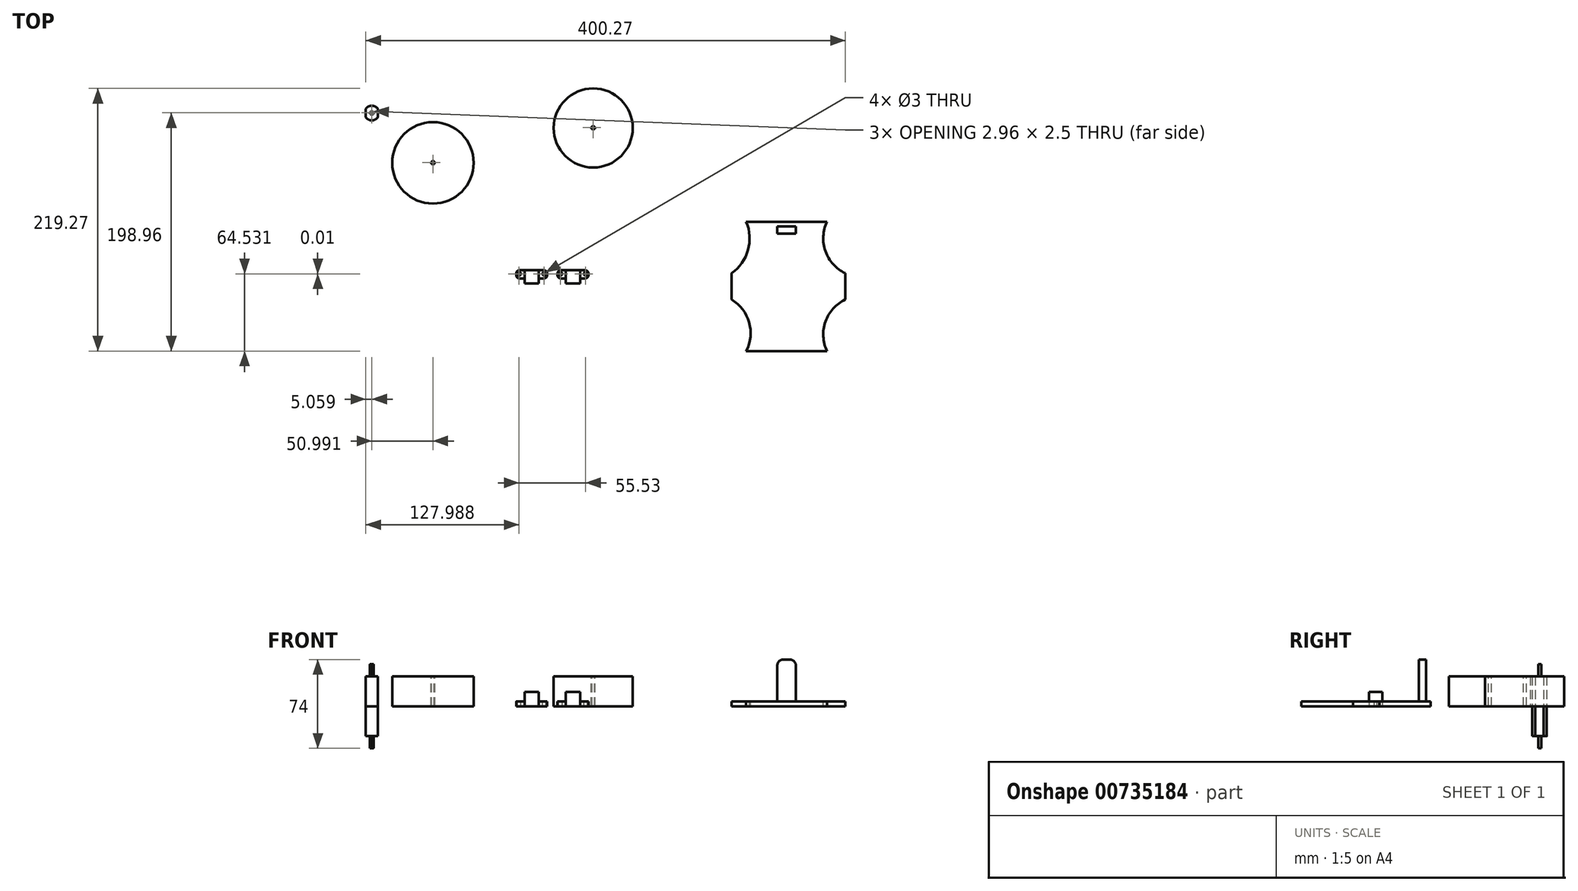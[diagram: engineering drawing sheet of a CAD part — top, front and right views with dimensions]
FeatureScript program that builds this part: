
annotation { "Feature Type Name" : "Feature", "Feature Type Description" : "" }
export const myFeature = defineFeature(function(context is Context, id is Id, definition is map)
    precondition{}
    {
        {
            var Q0;
            Q0=qCreatedBy(makeId("Top.planeOp"),FACE);
            var sketch = newSketch(context, id + "F0", { "sketchPlane" : qUnion([Q0])});
            skCircle(sketch, "E0", {"center": v(0, 0) * mm, "radius": 34 * mm});
            skSolve(sketch);
        }
        {
            var Q0;
            Q0=makeQuery(id+"F0.imprint","IMPRINT",FACE,{"disambiguationData":[TD([[makeQuery(id+"F0.imprint","IMPRINT",EDGE,{"derivedFrom":sQuery(id+"F0.wireOp",EDGE,"E0")}),1.0]])]});
            extrude(context, id + "F1", {"entities" : qUnion([Q0]), "depth" : 25 * mm, "offsetDistance" : 25 * mm});
        }
        {
            var Q0;
            Q0=qCreatedBy(makeId("Top.planeOp"),FACE);
            var sketch = newSketch(context, id + "F2", { "sketchPlane" : qUnion([Q0])});
            skArc(sketch, "E1", {"start": v(-56.05, 38.17) * mm, "mid": v(-51, 35.48) * mm, "end": v(-45.93, 38.17) * mm});
            skLineSegment(sketch, "E2", {"start": v(-56.05, 45) * mm, "end": v(-56.05, 38.17) * mm});
            skLineSegment(sketch, "E3", {"start": v(-45.93, 45) * mm, "end": v(-45.93, 38.17) * mm});
            skArc(sketch, "E4.trimOffspring", {"start": v(-45.93, 45) * mm, "mid": v(-51, 47.68) * mm, "end": v(-56.05, 45) * mm});
            skSolve(sketch);
        }
        {
            var Q0;
            Q0=makeQuery(id+"F1.opExtrude","CAP_FACE",FACE,{"disambiguationData":[OSD([sQuery(id+"F0.wireOp",EDGE,"E0")])],"isStart":false});
            var sketch = newSketch(context, id + "F3", { "sketchPlane" : qUnion([Q0])});
            skArc(sketch, "E5", {"start": v(1.12, -1) * mm, "mid": v(0, 1.5) * mm, "end": v(-1.12, -1) * mm});
            skLineSegment(sketch, "E6", {"start": v(0, -1) * mm, "end": v(-1.12, -1) * mm});
            skLineSegment(sketch, "E7", {"start": v(-1.12, -1) * mm, "end": v(1.12, -1) * mm});
            skSolve(sketch);
        }
        {
            var Q0;
            {var subQ0=sQuery(id+"F3.wireOp",EDGE,"E5");Q0=makeQuery(id+"F3.imprint","IMPRINT",FACE,{"disambiguationData":[TD([[makeQuery(id+"F3.imprint","IMPRINT",EDGE,{"derivedFrom":subQ0}),1.0]])]});}
            extrude(context, id + "F4", {"entities" : qUnion([Q0]), "operationType" : NewBodyOperationType.REMOVE, "oppositeDirection" : true, "depth" : 44 * mm, "offsetDistance" : 25 * mm});
        }
        {
            var Q0;
            Q0=makeQuery(id+"F2.imprint","IMPRINT",FACE,{"disambiguationData":[TD([[makeQuery(id+"F2.imprint","IMPRINT",EDGE,{"derivedFrom":sQuery(id+"F2.wireOp",EDGE,"E1")}),1.0]])]});
            extrude(context, id + "F5", {"entities" : qUnion([Q0]), "depth" : 25 * mm, "offsetDistance" : 25 * mm});
        }
        {
            var Q0;
            Q0=makeQuery(id+"F5.opExtrude","CAP_FACE",FACE,{"disambiguationData":[OSD([sQuery(id+"F2.wireOp",EDGE,"E1"),sQuery(id+"F2.wireOp",EDGE,"E2"),sQuery(id+"F2.wireOp",EDGE,"E3"),sQuery(id+"F2.wireOp",EDGE,"E4.trimOffspring")])],"isStart":false});
            var sketch = newSketch(context, id + "F6", { "sketchPlane" : qUnion([Q0])});
            skArc(sketch, "E8", {"start": v(-49.87, 40.58) * mm, "mid": v(-51, 43.08) * mm, "end": v(-52.1, 40.58) * mm});
            skLineSegment(sketch, "E9", {"start": v(-51, 40.58) * mm, "end": v(-52.1, 40.58) * mm});
            skLineSegment(sketch, "E10", {"start": v(-52.1, 40.58) * mm, "end": v(-49.87, 40.58) * mm});
            skSolve(sketch);
        }
        {
            var Q0;
            {var subQ0=sQuery(id+"F6.wireOp",EDGE,"E8");Q0=makeQuery(id+"F6.imprint","IMPRINT",FACE,{"disambiguationData":[TD([[makeQuery(id+"F6.imprint","IMPRINT",EDGE,{"derivedFrom":subQ0}),1.0]])]});}
            extrude(context, id + "F7", {"entities" : qUnion([Q0]), "operationType" : NewBodyOperationType.ADD, "depth" : 10 * mm, "offsetDistance" : 25 * mm});
        }
        {
            var Q0;
            Q0=qCreatedBy(makeId("Top.planeOp"),FACE);
            var sketch = newSketch(context, id + "F8", { "sketchPlane" : qUnion([Q0])});
            skCircle(sketch, "E11", {"center": v(133.78, 29.14) * mm, "radius": 33 * mm});
            skSolve(sketch);
        }
        {
            var Q0;
            Q0=makeQuery(id+"F8.imprint","IMPRINT",FACE,{"disambiguationData":[TD([[makeQuery(id+"F8.imprint","IMPRINT",EDGE,{"derivedFrom":sQuery(id+"F8.wireOp",EDGE,"E11")}),1.0]])]});
            extrude(context, id + "F9", {"entities" : qUnion([Q0]), "depth" : 25 * mm, "offsetDistance" : 25 * mm});
        }
        {
            var Q0;
            Q0=makeQuery(id+"F9.opExtrude","CAP_FACE",FACE,{"disambiguationData":[OSD([sQuery(id+"F8.wireOp",EDGE,"E11")])],"isStart":false});
            var sketch = newSketch(context, id + "F10", { "sketchPlane" : qUnion([Q0])});
            skArc(sketch, "E12", {"start": v(134.9, 28.14) * mm, "mid": v(133.78, 30.64) * mm, "end": v(132.66, 28.14) * mm});
            skLineSegment(sketch, "E13", {"start": v(133.77, 28.14) * mm, "end": v(132.66, 28.14) * mm});
            skLineSegment(sketch, "E14", {"start": v(132.66, 28.14) * mm, "end": v(134.9, 28.14) * mm});
            skSolve(sketch);
        }
        {
            var Q0;
            {var subQ0=sQuery(id+"F10.wireOp",EDGE,"E12");Q0=makeQuery(id+"F10.imprint","IMPRINT",FACE,{"disambiguationData":[TD([[makeQuery(id+"F10.imprint","IMPRINT",EDGE,{"derivedFrom":subQ0}),1.0]])]});}
            extrude(context, id + "F11", {"entities" : qUnion([Q0]), "operationType" : NewBodyOperationType.REMOVE, "oppositeDirection" : true, "depth" : 28.1 * mm, "offsetDistance" : 25 * mm});
        }
        {
            var Q0;
            Q0=makeQuery(id+"F5.opExtrude","SWEPT_BODY",BODY,{"disambiguationData":[OSD([sQuery(id+"F2.wireOp",EDGE,"E1"),sQuery(id+"F2.wireOp",EDGE,"E2"),sQuery(id+"F2.wireOp",EDGE,"E3"),sQuery(id+"F2.wireOp",EDGE,"E4.trimOffspring")])]});
            var Q1;
            Q1=qCreatedBy(makeId("Top.planeOp"),FACE);
            mirror(context, id + "F12", {"operationType" : NewBodyOperationType.ADD, "entities" : qUnion([Q0]), "mirrorPlane" : qUnion([Q1])});
        }
        {
            var Q0;
            Q0=qCreatedBy(makeId("Top.planeOp"),FACE);
            var sketch = newSketch(context, id + "F13", { "sketchPlane" : qUnion([Q0])});
            skLineSegment(sketch, "E15", {"start": v(249.22, -49.13) * mm, "end": v(249.22, -157.13) * mm});
            skLineSegment(sketch, "E16", {"start": v(249.22, -157.13) * mm, "end": v(344.22, -157.13) * mm});
            skLineSegment(sketch, "E17", {"start": v(344.22, -157.13) * mm, "end": v(344.22, -49.13) * mm});
            skLineSegment(sketch, "E18", {"start": v(249.22, -49.13) * mm, "end": v(344.22, -49.13) * mm});
            skSolve(sketch);
        }
        {
            var Q0;
            Q0=makeQuery(id+"F13.imprint","IMPRINT",FACE,{"disambiguationData":[TD([[makeQuery(id+"F13.imprint","IMPRINT",EDGE,{"derivedFrom":sQuery(id+"F13.wireOp",EDGE,"E15")}),1.0]])]});
            extrude(context, id + "F14", {"entities" : qUnion([Q0]), "depth" : 4 * mm, "offsetDistance" : 25 * mm});
        }
        {
            var Q0;
            Q0=makeQuery(id+"F14.opExtrude","CAP_FACE",FACE,{"disambiguationData":[OSD([sQuery(id+"F13.wireOp",EDGE,"E15"),sQuery(id+"F13.wireOp",EDGE,"E16"),sQuery(id+"F13.wireOp",EDGE,"E17"),sQuery(id+"F13.wireOp",EDGE,"E18")])],"isStart":false});
            var sketch = newSketch(context, id + "F15", { "sketchPlane" : qUnion([Q0])});
            skLineSegment(sketch, "E19", {"start": v(249.22, -49.13) * mm, "end": v(249.22, -92.13) * mm});
            skLineSegment(sketch, "E20", {"start": v(296.72, -49.13) * mm, "end": v(261.47, -49.13) * mm});
            skArc(sketch, "E21", {"start": v(249.22, -92.13) * mm, "mid": v(263.03, -72.82) * mm, "end": v(261.47, -49.13) * mm});
            skLineSegment(sketch, "E22", {"start": v(344.22, -49.13) * mm, "end": v(344.22, -92.13) * mm});
            skLineSegment(sketch, "E23", {"start": v(296.72, -49.13) * mm, "end": v(328.97, -49.13) * mm});
            skArc(sketch, "E24", {"start": v(328.97, -49.13) * mm, "mid": v(327.68, -73.8) * mm, "end": v(344.22, -92.13) * mm});
            skArc(sketch, "E25", {"start": v(261.47, -157.13) * mm, "mid": v(264, -133.17) * mm, "end": v(249.22, -114.13) * mm});
            skLineSegment(sketch, "E26", {"start": v(261.47, -157.13) * mm, "end": v(326.68, -157.13) * mm});
            skLineSegment(sketch, "E27", {"start": v(328.97, -157.13) * mm, "end": v(326.68, -157.13) * mm});
            skArc(sketch, "E28", {"start": v(344.22, -114.13) * mm, "mid": v(327.68, -132.47) * mm, "end": v(328.97, -157.13) * mm});
            skSolve(sketch);
        }
        {
            var Q0;
            {var subQ0=sQuery(id+"F15.wireOp",EDGE,"E19");Q0=makeQuery(id+"F15.imprint","IMPRINT",FACE,{"disambiguationData":[TD([[makeQuery(id+"F15.imprint","IMPRINT",EDGE,{"derivedFrom":subQ0}),1.0]])]});}
            var Q1;
            {var subQ0=sQuery(id+"F15.wireOp",EDGE,"E22");Q1=makeQuery(id+"F15.imprint","IMPRINT",FACE,{"disambiguationData":[TD([[makeQuery(id+"F15.imprint","IMPRINT",EDGE,{"derivedFrom":subQ0}),1.0]])]});}
            var Q2;
            {var subQ0=sQuery(id+"F15.wireOp",EDGE,"E28");Q2=makeQuery(id+"F15.imprint","IMPRINT",FACE,{"disambiguationData":[TD([[makeQuery(id+"F15.imprint","IMPRINT",EDGE,{"derivedFrom":subQ0}),1.0]])]});}
            var Q3;
            {var subQ0=sQuery(id+"F15.wireOp",EDGE,"E25");Q3=makeQuery(id+"F15.imprint","IMPRINT",FACE,{"disambiguationData":[TD([[makeQuery(id+"F15.imprint","IMPRINT",EDGE,{"derivedFrom":subQ0}),1.0]])]});}
            extrude(context, id + "F16", {"entities" : qUnion([Q0, Q1, Q2, Q3]), "operationType" : NewBodyOperationType.REMOVE, "oppositeDirection" : true, "depth" : 25 * mm, "offsetDistance" : 25 * mm});
        }
        {
            var Q0;
            Q0=makeQuery(id+"F14.opExtrude","CAP_FACE",FACE,{"disambiguationData":[OSD([sQuery(id+"F13.wireOp",EDGE,"E15"),sQuery(id+"F13.wireOp",EDGE,"E16"),sQuery(id+"F13.wireOp",EDGE,"E17"),sQuery(id+"F13.wireOp",EDGE,"E18")])],"isStart":false});
            var sketch = newSketch(context, id + "F17", { "sketchPlane" : qUnion([Q0])});
            skLineSegment(sketch, "E29", {"start": v(328.97, -49.13) * mm, "end": v(302.97, -49.13) * mm});
            skLineSegment(sketch, "E30", {"start": v(261.47, -49.13) * mm, "end": v(287.47, -49.13) * mm});
            skLineSegment(sketch, "E31", {"start": v(287.47, -53.13) * mm, "end": v(287.47, -59.13) * mm});
            skLineSegment(sketch, "E32", {"start": v(287.47, -59.13) * mm, "end": v(302.97, -59.13) * mm});
            skLineSegment(sketch, "E33", {"start": v(287.47, -53.13) * mm, "end": v(302.97, -53.13) * mm});
            skLineSegment(sketch, "E34", {"start": v(302.97, -53.13) * mm, "end": v(302.97, -59.13) * mm});
            skSolve(sketch);
        }
        {
            var Q0;
            Q0=makeQuery(id+"F17.imprint","IMPRINT",FACE,{"disambiguationData":[TD([[makeQuery(id+"F17.imprint","IMPRINT",EDGE,{"derivedFrom":sQuery(id+"F17.wireOp",EDGE,"E31")}),1.0]])]});
            extrude(context, id + "F18", {"entities" : qUnion([Q0]), "operationType" : NewBodyOperationType.ADD, "depth" : 35 * mm, "offsetDistance" : 25 * mm});
        }
        {
            var Q0;
            Q0=makeQuery(id+"F18.opExtrude","CAP_EDGE",EDGE,{"disambiguationData":[OSD([sQuery(id+"F17.wireOp",EDGE,"E31")])],"isStart":false});
            var Q1;
            Q1=makeQuery(id+"F18.opExtrude","CAP_EDGE",EDGE,{"disambiguationData":[OSD([sQuery(id+"F17.wireOp",EDGE,"E34")])],"isStart":false});
            fillet(context, id + "F19", {"entities" : qUnion([Q0, Q1]), "radius" : 5 * mm, "tangentPropagation" : true, "allowEdgeOverflow" : false});
        }
        {
            var Q0;
            Q0=qCreatedBy(makeId("Top.planeOp"),FACE);
            var sketch = newSketch(context, id + "F20", { "sketchPlane" : qUnion([Q0])});
            skLineSegment(sketch, "E35", {"start": v(76.44, -100.59) * mm, "end": v(88.44, -100.59) * mm});
            skLineSegment(sketch, "E36", {"start": v(88.44, -100.59) * mm, "end": v(88.44, -96.59) * mm});
            skLineSegment(sketch, "E37", {"start": v(88.44, -96.59) * mm, "end": v(95.44, -96.59) * mm});
            skLineSegment(sketch, "E38", {"start": v(95.44, -96.59) * mm, "end": v(95.44, -89.59) * mm});
            skLineSegment(sketch, "E39", {"start": v(76.44, -100.59) * mm, "end": v(76.44, -96.59) * mm});
            skLineSegment(sketch, "E40", {"start": v(76.44, -96.59) * mm, "end": v(69.44, -96.59) * mm});
            skLineSegment(sketch, "E41", {"start": v(69.44, -96.59) * mm, "end": v(69.44, -89.59) * mm});
            skLineSegment(sketch, "E42", {"start": v(69.44, -89.59) * mm, "end": v(95.44, -89.59) * mm});
            skPoint(sketch, "E43.endSnap0", {"position": v(82.44, -89.59) * mm});
            skSolve(sketch);
        }
        {
            var Q0;
            Q0=makeQuery(id+"F20.imprint","IMPRINT",FACE,{"disambiguationData":[TD([[makeQuery(id+"F20.imprint","IMPRINT",EDGE,{"derivedFrom":sQuery(id+"F20.wireOp",EDGE,"E35")}),1.0]])]});
            extrude(context, id + "F21", {"entities" : qUnion([Q0]), "depth" : 12 * mm, "offsetDistance" : 25 * mm});
        }
        {
            var Q0;
            Q0=makeQuery(id+"F21.opExtrude","CAP_FACE",FACE,{"disambiguationData":[OSD([sQuery(id+"F20.wireOp",EDGE,"E35"),sQuery(id+"F20.wireOp",EDGE,"E36"),sQuery(id+"F20.wireOp",EDGE,"E37"),sQuery(id+"F20.wireOp",EDGE,"E38"),sQuery(id+"F20.wireOp",EDGE,"E39"),sQuery(id+"F20.wireOp",EDGE,"E40"),sQuery(id+"F20.wireOp",EDGE,"E41"),sQuery(id+"F20.wireOp",EDGE,"E42")])],"isStart":false});
            var sketch = newSketch(context, id + "F22", { "sketchPlane" : qUnion([Q0])});
            skLineSegment(sketch, "E44", {"start": v(88.44, -96.59) * mm, "end": v(88.44, -89.59) * mm});
            skLineSegment(sketch, "E45", {"start": v(76.44, -96.59) * mm, "end": v(76.44, -89.59) * mm});
            skSolve(sketch);
        }
        {
            var Q0;
            {var subQ0=sQuery(id+"F22.wireOp",EDGE,"E44");Q0=makeQuery(id+"F22.imprint","IMPRINT",FACE,{"disambiguationData":[TD([[makeQuery(id+"F22.imprint","IMPRINT",EDGE,{"derivedFrom":subQ0}),-1.0]])]});}
            var Q1;
            {var subQ0=sQuery(id+"F22.wireOp",EDGE,"E45");Q1=makeQuery(id+"F22.imprint","IMPRINT",FACE,{"disambiguationData":[TD([[makeQuery(id+"F22.imprint","IMPRINT",EDGE,{"derivedFrom":subQ0}),1.0]])]});}
            extrude(context, id + "F23", {"entities" : qUnion([Q0, Q1]), "operationType" : NewBodyOperationType.REMOVE, "oppositeDirection" : true, "depth" : 8 * mm, "offsetDistance" : 25 * mm});
        }
        {
            var Q0;
            Q0=makeQuery(id+"F21.opExtrude","SWEPT_EDGE",EDGE,{"disambiguationData":[OSD([sQuery(id+"F20.wireOp",EDGE,"E38"),sQuery(id+"F20.wireOp",EDGE,"E42")])]});
            var Q1;
            Q1=makeQuery(id+"F21.opExtrude","SWEPT_EDGE",EDGE,{"disambiguationData":[OSD([sQuery(id+"F20.wireOp",EDGE,"E37"),sQuery(id+"F20.wireOp",EDGE,"E38")])]});
            var Q2;
            Q2=makeQuery(id+"F21.opExtrude","SWEPT_EDGE",EDGE,{"disambiguationData":[OSD([sQuery(id+"F20.wireOp",EDGE,"E40"),sQuery(id+"F20.wireOp",EDGE,"E41")])]});
            var Q3;
            Q3=makeQuery(id+"F21.opExtrude","SWEPT_EDGE",EDGE,{"disambiguationData":[OSD([sQuery(id+"F20.wireOp",EDGE,"E41"),sQuery(id+"F20.wireOp",EDGE,"E42")])]});
            fillet(context, id + "F24", {"entities" : qUnion([Q0, Q1, Q2, Q3]), "radius" : 3 * mm, "tangentPropagation" : true, "allowEdgeOverflow" : false});
        }
        {
            var Q0;
            Q0=makeQuery(id+"F23.boolean.opBoolean","COPY",FACE,{"derivedFrom":makeQuery(id+"F23.opExtrude","CAP_FACE",FACE,{"disambiguationData":[OSD([sQuery(id+"F20.wireOp",EDGE,"E37"),sQuery(id+"F20.wireOp",EDGE,"E38"),sQuery(id+"F20.wireOp",EDGE,"E42"),sQuery(id+"F22.wireOp",EDGE,"E44")])],"isStart":false})});
            var sketch = newSketch(context, id + "F25", { "sketchPlane" : qUnion([Q0])});
            skCircle(sketch, "E46", {"center": v(92.94, -92.59) * mm, "radius": 1.5 * mm});
            skSolve(sketch);
        }
        {
            var Q0;
            Q0=makeQuery(id+"F23.boolean.opBoolean","COPY",FACE,{"derivedFrom":makeQuery(id+"F23.opExtrude","CAP_FACE",FACE,{"disambiguationData":[OSD([sQuery(id+"F20.wireOp",EDGE,"E40"),sQuery(id+"F20.wireOp",EDGE,"E41"),sQuery(id+"F20.wireOp",EDGE,"E42"),sQuery(id+"F22.wireOp",EDGE,"E45")])],"isStart":false})});
            var sketch = newSketch(context, id + "F26", { "sketchPlane" : qUnion([Q0])});
            skCircle(sketch, "E47", {"center": v(71.94, -92.59) * mm, "radius": 1.5 * mm});
            skSolve(sketch);
        }
        {
            var Q0;
            Q0=makeQuery(id+"F26.imprint","IMPRINT",FACE,{"disambiguationData":[TD([[makeQuery(id+"F26.imprint","IMPRINT",EDGE,{"derivedFrom":sQuery(id+"F26.wireOp",EDGE,"E47")}),1.0]])]});
            var Q1;
            Q1=makeQuery(id+"F25.imprint","IMPRINT",FACE,{"disambiguationData":[TD([[makeQuery(id+"F25.imprint","IMPRINT",EDGE,{"derivedFrom":sQuery(id+"F25.wireOp",EDGE,"E46")}),1.0]])]});
            extrude(context, id + "F27", {"entities" : qUnion([Q0, Q1]), "operationType" : NewBodyOperationType.REMOVE, "oppositeDirection" : true, "depth" : 25 * mm, "offsetDistance" : 25 * mm});
        }
        {
            var Q0;
            Q0=qCreatedBy(makeId("Top.planeOp"),FACE);
            var sketch = newSketch(context, id + "F28", { "sketchPlane" : qUnion([Q0])});
            skLineSegment(sketch, "E48", {"start": v(110.97, -100.6) * mm, "end": v(122.97, -100.6) * mm});
            skLineSegment(sketch, "E49", {"start": v(122.97, -100.6) * mm, "end": v(122.97, -96.6) * mm});
            skLineSegment(sketch, "E50", {"start": v(110.97, -100.6) * mm, "end": v(110.97, -96.6) * mm});
            skLineSegment(sketch, "E51", {"start": v(110.97, -96.6) * mm, "end": v(103.97, -96.6) * mm});
            skLineSegment(sketch, "E52", {"start": v(103.97, -96.6) * mm, "end": v(103.97, -89.6) * mm});
            skLineSegment(sketch, "E53", {"start": v(103.97, -89.6) * mm, "end": v(129.97, -89.6) * mm});
            skLineSegment(sketch, "E54", {"start": v(129.97, -89.6) * mm, "end": v(129.97, -96.6) * mm});
            skLineSegment(sketch, "E55", {"start": v(122.97, -96.6) * mm, "end": v(129.97, -96.6) * mm});
            skSolve(sketch);
        }
        {
            var Q0;
            Q0=makeQuery(id+"F28.imprint","IMPRINT",FACE,{"disambiguationData":[TD([[makeQuery(id+"F28.imprint","IMPRINT",EDGE,{"derivedFrom":sQuery(id+"F28.wireOp",EDGE,"E48")}),1.0]])]});
            extrude(context, id + "F29", {"entities" : qUnion([Q0]), "depth" : 12 * mm, "offsetDistance" : 25 * mm});
        }
        {
            var Q0;
            Q0=makeQuery(id+"F29.opExtrude","CAP_FACE",FACE,{"disambiguationData":[OSD([sQuery(id+"F28.wireOp",EDGE,"E48"),sQuery(id+"F28.wireOp",EDGE,"E49"),sQuery(id+"F28.wireOp",EDGE,"E50"),sQuery(id+"F28.wireOp",EDGE,"E51"),sQuery(id+"F28.wireOp",EDGE,"E52"),sQuery(id+"F28.wireOp",EDGE,"E53"),sQuery(id+"F28.wireOp",EDGE,"E54"),sQuery(id+"F28.wireOp",EDGE,"E55")])],"isStart":false});
            var sketch = newSketch(context, id + "F30", { "sketchPlane" : qUnion([Q0])});
            skLineSegment(sketch, "E56", {"start": v(110.97, -96.6) * mm, "end": v(110.97, -89.6) * mm});
            skLineSegment(sketch, "E57", {"start": v(122.97, -96.6) * mm, "end": v(122.97, -89.6) * mm});
            skSolve(sketch);
        }
        {
            var Q0;
            {var subQ0=sQuery(id+"F30.wireOp",EDGE,"E57");Q0=makeQuery(id+"F30.imprint","IMPRINT",FACE,{"disambiguationData":[TD([[makeQuery(id+"F30.imprint","IMPRINT",EDGE,{"derivedFrom":subQ0}),-1.0]])]});}
            var Q1;
            {var subQ0=sQuery(id+"F30.wireOp",EDGE,"E56");Q1=makeQuery(id+"F30.imprint","IMPRINT",FACE,{"disambiguationData":[TD([[makeQuery(id+"F30.imprint","IMPRINT",EDGE,{"derivedFrom":subQ0}),1.0]])]});}
            extrude(context, id + "F31", {"entities" : qUnion([Q0, Q1]), "operationType" : NewBodyOperationType.REMOVE, "oppositeDirection" : true, "depth" : 8 * mm, "offsetDistance" : 25 * mm});
        }
        {
            var Q0;
            Q0=makeQuery(id+"F29.opExtrude","SWEPT_EDGE",EDGE,{"disambiguationData":[OSD([sQuery(id+"F28.wireOp",EDGE,"E53"),sQuery(id+"F28.wireOp",EDGE,"E54")])]});
            var Q1;
            Q1=makeQuery(id+"F29.opExtrude","SWEPT_EDGE",EDGE,{"disambiguationData":[OSD([sQuery(id+"F28.wireOp",EDGE,"E54"),sQuery(id+"F28.wireOp",EDGE,"E55")])]});
            fillet(context, id + "F32", {"entities" : qUnion([Q0, Q1]), "radius" : 3 * mm, "tangentPropagation" : true, "allowEdgeOverflow" : false});
        }
        {
            var Q0;
            Q0=makeQuery(id+"F29.opExtrude","SWEPT_EDGE",EDGE,{"disambiguationData":[OSD([sQuery(id+"F28.wireOp",EDGE,"E51"),sQuery(id+"F28.wireOp",EDGE,"E52")])]});
            var Q1;
            Q1=makeQuery(id+"F29.opExtrude","SWEPT_EDGE",EDGE,{"disambiguationData":[OSD([sQuery(id+"F28.wireOp",EDGE,"E52"),sQuery(id+"F28.wireOp",EDGE,"E53")])]});
            fillet(context, id + "F33", {"entities" : qUnion([Q0, Q1]), "radius" : 3 * mm, "tangentPropagation" : true, "allowEdgeOverflow" : false});
        }
        {
            var Q0;
            Q0=makeQuery(id+"F31.boolean.opBoolean","COPY",FACE,{"derivedFrom":makeQuery(id+"F31.opExtrude","CAP_FACE",FACE,{"disambiguationData":[OSD([sQuery(id+"F28.wireOp",EDGE,"E51"),sQuery(id+"F28.wireOp",EDGE,"E52"),sQuery(id+"F28.wireOp",EDGE,"E53"),sQuery(id+"F30.wireOp",EDGE,"E56")])],"isStart":false})});
            var sketch = newSketch(context, id + "F34", { "sketchPlane" : qUnion([Q0])});
            skCircle(sketch, "E58", {"center": v(106.47, -92.6) * mm, "radius": 1.5 * mm});
            skSolve(sketch);
        }
        {
            var Q0;
            Q0=makeQuery(id+"F31.boolean.opBoolean","COPY",FACE,{"derivedFrom":makeQuery(id+"F31.opExtrude","CAP_FACE",FACE,{"disambiguationData":[OSD([sQuery(id+"F28.wireOp",EDGE,"E53"),sQuery(id+"F28.wireOp",EDGE,"E54"),sQuery(id+"F28.wireOp",EDGE,"E55"),sQuery(id+"F30.wireOp",EDGE,"E57")])],"isStart":false})});
            var sketch = newSketch(context, id + "F35", { "sketchPlane" : qUnion([Q0])});
            skCircle(sketch, "E59", {"center": v(127.47, -92.6) * mm, "radius": 1.5 * mm});
            skSolve(sketch);
        }
        {
            var Q0;
            Q0=makeQuery(id+"F34.imprint","IMPRINT",FACE,{"disambiguationData":[TD([[makeQuery(id+"F34.imprint","IMPRINT",EDGE,{"derivedFrom":sQuery(id+"F34.wireOp",EDGE,"E58")}),1.0]])]});
            var Q1;
            Q1=makeQuery(id+"F35.imprint","IMPRINT",FACE,{"disambiguationData":[TD([[makeQuery(id+"F35.imprint","IMPRINT",EDGE,{"derivedFrom":sQuery(id+"F35.wireOp",EDGE,"E59")}),1.0]])]});
            extrude(context, id + "F36", {"entities" : qUnion([Q0, Q1]), "operationType" : NewBodyOperationType.REMOVE, "oppositeDirection" : true, "depth" : 25 * mm, "offsetDistance" : 25 * mm});
        }
    });
